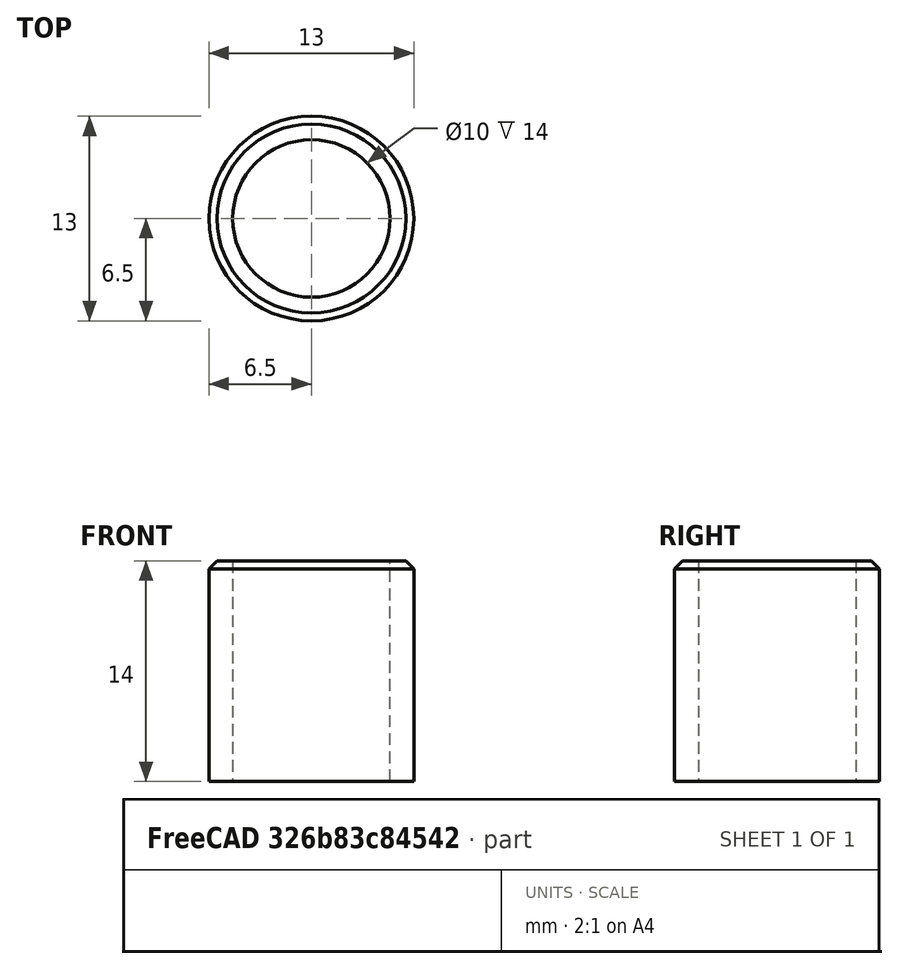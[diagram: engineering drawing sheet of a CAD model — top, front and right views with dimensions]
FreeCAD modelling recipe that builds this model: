
FCSTD DOCUMENT  (FreeCAD 0.19R24276 (Git))
Label: roller_16x24_in_part
License: All rights reserved
LicenseURL: http://en.wikipedia.org/wiki/All_rights_reserved
objects: Sketcher::SketchObject×1, PartDesign::Pad×1, PartDesign::Chamfer×1, PartDesign::Body×1
note: 6 computed .brp shape members not serialized (recipe doc carries the construction recipe); baked Part::Feature solids carry a one-line shape summary decoded from their .brp

FEATURE [Sketcher::SketchObject] Sketch
  FullyConstrained = true
  MapMode = 5
  Support = -> [XY_Plane]
  sketch-geometry (2):
    g0: Circle CenterX=0 CenterY=0 CenterZ=0 NormalX=0 NormalY=0 NormalZ=1 AngleXU=0 Radius=6.5
    g1: Circle CenterX=0 CenterY=0 CenterZ=0 NormalX=0 NormalY=0 NormalZ=1 AngleXU=0 Radius=5
  constraints (4):
    c: Coincident(g0,g-1)
    c: Coincident(g1,g0)
    c: Diameter(g0) = 13
    c: Diameter(g1) = 10
FEATURE [PartDesign::Pad] Pad
  Direction = (1,1,1)
  Length = 14
  Length2 = 100
  Profile = -> Sketch
  Type = 0
FEATURE [PartDesign::Chamfer] Chamfer
  Angle = 45
  Base = -> Pad [Edge3]
  BaseFeature = -> Pad
  ChamferType = 0
  FlipDirection = false
  Size = 0.5
  Size2 = 1
  SupportTransform = false
FEATURE [PartDesign::Body] Body
  Group = -> [Sketch,Pad,Chamfer]
  Origin = -> Origin
  Tip = -> Chamfer
